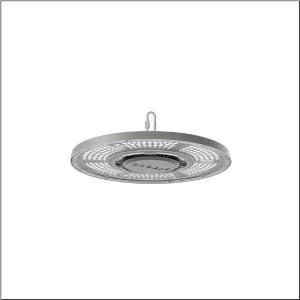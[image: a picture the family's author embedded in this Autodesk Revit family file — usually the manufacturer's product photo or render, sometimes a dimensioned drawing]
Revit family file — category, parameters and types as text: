
# Revit family: highbay_31-l_51hc41da4jmb
name_source: partatom
category: Lighting Fixtures
units: mm (PartAtom-declared; Revit-internal decimal feet)

## family parameters
Cut with Voids When Loaded = No
Host = Face
Light Source = No
Part Type = Normal
Room Calculation Point = No
Round Connector Dimension = Use Diameter
Shared = No

## types (1)
- Highbay 31-L (1 x LED, 20000 lm, 134 W, 4000K)
    Apparent Load = 134 VA
    CIE Flux Codes = 95 98 100 100 100
    Color Rendering = 80
    Color Temperature = 4000K
    Default Elevation = 1800 mm
    Description = Highbay 31-L, LED high bay luminaire, primary light control with lens, of PC, primary optical cover: cover panel, of PC, transparent, light emission: direct distribution, primary light characteristic: rotationally symmetric, installation type: suspended mounting, surface-mounted, LED, rated luminous flux: 20.000lm, luminous efficacy: 150lm/W, light colour: 840, colour temperature: 4000K, control gear: ECG DALI, with cable, 5x 1.0mm², free wire ends, mains connection: 220..240V, AC/DC, 0/50..60Hz, cable length: 1,5m, rated input power: 134W, housing, rotationally symmetric, of diecast aluminium, powder-coated, grey aluminium (RAL 9007), with hook on luminaire side, incl. screw, diameter: 404mm, protection rating (complete): IP65, insulation class (complete): insulation class I (protective earthing), certification: CE, ENEC, UKCA, protection symbol: D, impact resistance: IK08, permissible operating ambient temperature: -30..+45°C, standard: EN 60598-2-22, EN 60598, corresponds to IFS (International Featured Standards) requirements for safety and quality in the food industry, packaging unit: 1 piece
    Height = 141 mm
    Lamp = 1 x LED
    Lamp Light Flux = 20000 lm
    Lamp Power = 134 W
    Lamp count = 1
    Length = 406 mm
    Luminous efficacy = 149 lm/W
    Manufacturer = Siteco
    ModVariant = No
    Model = 51HC41DA4JMB
    Mounting Place = Ceiling
    Mounting Type = Pendant
    Number of Poles = 1
    OnlyDefault = Yes
    Power Factor = 1
    Product Name = Highbay 31-L
    Product group = LED high bay luminaire
    ProductGroupID = 903
    Protection Class = Protection class I
    Protection Degree = IP 65
    RLX_Detail_Level = 1
    RLX_Emergency_Light_Flux = 0 lm
    RLX_Emergency_Type = 0
    RLX_Emergency_Type_DB = No
    RlxData = <blob elided: 108025 chars, md5=5a8b132a>
    Socket = socket
    Standby Power = 0 W
    System Light Flux = 20000 lm
    System Power = 134 W
    Type Comments = Product without accessories
    Type Image = l_1007237.jpg
    URL = http://relux.com
    VarID = ---
    Voltage = 0 V
    Weight = 0.00 kg
    Width = 0 mm  [stored 0 ft]

note: [stored X ft] marks values corroborated as IEEE doubles in the binary element streams (Revit-internal decimal feet)

## geometry (parser evidence)
native form markers: Blend x4, Sweep x10
no freeform markers — native parametric forms only
